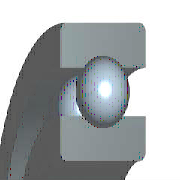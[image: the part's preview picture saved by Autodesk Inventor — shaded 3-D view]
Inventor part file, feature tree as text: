
AUTODESK INVENTOR PART (.ipt)
format: ipt  version: 2023.1 (Build 271208000, 208)  size: 340,480 bytes
history: native  units: mm (DEFAULTED — no unit token found)
features: sketch x5, other x3, plane x2, pattern_circular x1, fillet x1
ambient origin geometry x8: Origin, YZ Plane, XZ Plane, XY Plane, X Axis, Y Axis, Z Axis, Center Point
bodies: Solid1 (feature_tree)
feature tree (12):
  sketch  "Sketch1"  dims[d2=72.0mm]
  other  "WorkPoint1"
  other  "WorkAxis1"
  plane  "WorkPlane3"
  plane  "WorkPlane4"
  sketch  "Sketch4"  dims[d5=31.0mm]
  other  "WorkPoint2"
  pattern_circular  "PolarArray1"  Count=2  [1 undecoded]
  fillet  "Fillet1"  Radius=60.0mm
  sketch  "Sketch2"  dims[d3=130.0mm]
  sketch  "Sketch3"  dims[d4=19.0mm]
  sketch  "Sketch5"  dims[d6=360.0deg d7=0.0mm d8=15.6mm d9=21.0mm d10=360.0deg d11=-31.0mm d12=0.0mm d13=0.0mm d14=15.6001mm d15=21.0001mm d16=360.0deg d17=71.857143mm d19=360.0deg d20=2.1mm d21=41.2mm d22=47.5mm d23=53.8mm d26=0.0mm d27=0.0mm d28=0.0mm d29=0.0mm d30=0.0mm]
note: 1 required parameter value undecoded (feature->parameter linkage not recoverable at this tier; creation-order binding heuristic only, values carry confidence <= 0.55)
